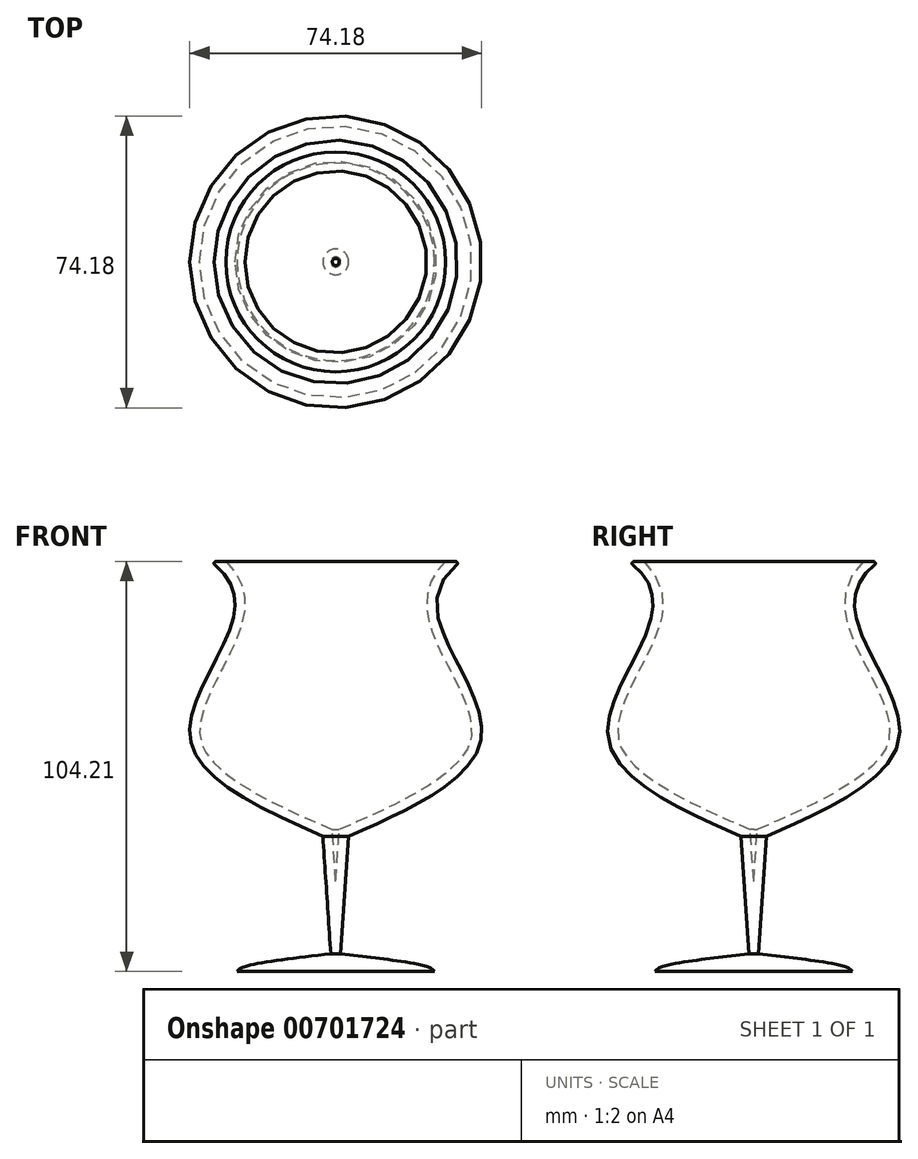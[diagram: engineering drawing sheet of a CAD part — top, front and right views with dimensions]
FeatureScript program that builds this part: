
annotation { "Feature Type Name" : "Feature", "Feature Type Description" : "" }
export const myFeature = defineFeature(function(context is Context, id is Id, definition is map)
    precondition{}
    {
        {
            var Q0;
            Q0=qCreatedBy(makeId("Front.planeOp"),FACE);
            var sketch = newSketch(context, id + "F0", { "sketchPlane" : qUnion([Q0])});
            skLineSegment(sketch, "E0", {"start": v(0, 44.57) * mm, "end": v(-31.9, 44.57) * mm});
            skFitSpline(sketch, "E1", {"points": [v(-31.9, 44.57) * mm, v(-26.52, 28.45) * mm, v(-37, 0) * mm, v(-3.28, -25.25) * mm], "startDerivative": vector(73.07, -51.23) * mm, "endDerivative": vector(132.31, -57.4) * mm});
            skLineSegment(sketch, "E2", {"start": v(-3.28, -25.25) * mm, "end": v(-1.25, -55.14) * mm});
            skFitSpline(sketch, "E3", {"points": [v(-1.25, -55.14) * mm, v(-23.71, -58.6) * mm, v(-25.08, -59.64) * mm], "startDerivative": vector(-37.38, -4.25) * mm, "endDerivative": vector(-3.95, -4.88) * mm});
            skLineSegment(sketch, "E4", {"start": v(-25.08, -59.64) * mm, "end": v(0, -59.64) * mm});
            skLineSegment(sketch, "E5", {"start": v(0, -59.64) * mm, "end": v(0, 44.57) * mm});
            skSolve(sketch);
        }
        {
            var Q0;
            Q0 = qSketchRegion(id + "F0", true);
            var Q1;
            Q1=sQuery(id+"F0.wireOp",EDGE,"E5");
            revolve(context, id + "F1", {"surfaceOperationType" : NewSurfaceOperationType.NEW, "entities" : qUnion([Q0]), "axis" : qUnion([Q1]), "revolveType" : RevolveType.FULL});
        }
        {
            var Q0;
            Q0=makeQuery(id+"F1.opRevolve","SWEPT_EDGE",EDGE,{"disambiguationData":[OSD([sQuery(id+"F0.wireOp",EDGE,"E0"),sQuery(id+"F0.wireOp",EDGE,"E1")])]});
            fillet(context, id + "F2", {"entities" : qUnion([Q0]), "radius" : .5 * mm, "tangentPropagation" : true, "allowEdgeOverflow" : false});
        }
        {
            var Q0;
            Q0=makeQuery(id+"F1.opRevolve","SWEPT_FACE",FACE,{"disambiguationData":[OSD([sQuery(id+"F0.wireOp",EDGE,"E0")])]});
            shell(context, id + "F3", {"entities" : qUnion([Q0]), "thickness" : 2.5 * mm});
        }
    });
